# Revit family: STH8541_27
name_source: partatom
category: Luminárias
units: mm (PartAtom-declared; Revit-internal decimal feet)

## family parameters
Com base no plano de trabalho = Não
Compartilhado = Não
Corte com vazios quando carregada = Não
Cota do conector redondo = Utilizar diâmetro
Fonte luminosa = Sim
Manter orientação da anotação = Não
Ponto de cálculo do ambiente = Não
Sempre na vertical = Sim
Tipo de parte = Normal

## types (1)
- STH8541/27 - 127V - 2700K - 460lm - 36°
    Altura = 0.05 m
    Arquivo de rede fotométrica = STELLA - STH8541-27 - DICROICA 6W DIM.ies
    Cromado = Cromado
    Dimerização = 20-100%
    Diâmetro = 0.05 m
    Elevação padrão = 0 m
    Fabricante = Stella
    Filtro de cor = 16777215
    Fluxo Luminoso = 460 lm
    Grau de proteção (IP) = IP20
    IRC (Índice de reprodução de cores) = >80
    Modelo = Dicroica MR16 ECO - Dimerizável
AR70 PRO 7º 4,7W
AR 70 PRO 7º 4,7W
    Potência = 6 W
    Referência = STH8541/27 - 127V
    Temperatura da cor (K) = 2700 K
    Tensão Elétrica = 127V
    Troca de temperatura da cor de lâmpada com esmaecimento = <Nenhum>
    URL = https://stella.com.br
    Vidro = Vidro
    Ângulo de Abertura = 36º
    Ângulo de inclinação = 90.00°
